# Revit family: Faucet-Kitchen-KOHLER-Crue-K-22974_1
name_source: partatom
category: Plumbing Fixtures
revit_build: Autodesk Revit 2017 (Build: 20160225_1515(x64)
units: mm (PartAtom-declared; Revit-internal decimal feet)

## family parameters
Cut with Voids When Loaded = No
Host = Face
OmniClass Number = 23.31.11.00
OmniClass Title = Faucets
Part Type = Normal
Room Calculation Point = No
Round Connector Dimension = Use Diameter
Shared = No

## types (4) — shared parameters
ADA Compliant = Yes
Apparent Load = 18 VA
Assembly Code = D2010
CW Connection = Yes
Cold Water Inlet = Cold Water Inlet
Date Modified = 07/01/2020
Default Elevation = 36"
Description = Touchless Pulldown Kitchen Faucet
Drain Included = No
Electrical Connector = Yes
Electrical Note = One Dedicated Circuit Required
Flow Rate = 2 GPM
HW Connection = Yes
Handle Clearance = 2 3/4"
Height = 17 3/16"
Hot Water Inlet = Hot Water Inlet
Length = 8 9/16"
Manufacturer = KOHLER Co.
Master Format 2014 = 22 41 39
Master Format 2014 Name = Residential Faucets, Supplies, and Trim
Material = Premium Metal Construction
Pressure = 60.00 psi
Product Documentation Link = https://www.us.kohler.com
Product Name = Crue
Product Page URL = http://www.us.kohler.com
Spout Reach = 8 9/16"
URL = https://www.us.kohler.com
Vent Connection = No
Voltage = 120 V
Waste Connection = No
Waste Water Outlet = Waste Water Outlet
WaterSense Certified = No

## per-type parameters (varying)
| type | Finish | Model | Type |
| CP-Polished Chrome | Kohler-Metal-CP-Polished_Chrome | K-22974-CP | 1 |
| VS-Vibrant Stainless | Kohler-Metal-VS-Vibrant_Stainless | K-22974-VS | 2 |
| 2MB-Vibrant Brushed Moderne Brass | Kohler-Metal-2MB-Vibrant_Brushed_Moderne_Brass | K-22974-2MB | 3 |
| BL-Matte Black | Kohler-Metal-BL-Matte_Black | K-22974-BL | 4 |

## geometry (parser evidence)
native form markers: Sweep x9
no freeform markers — native parametric forms only
